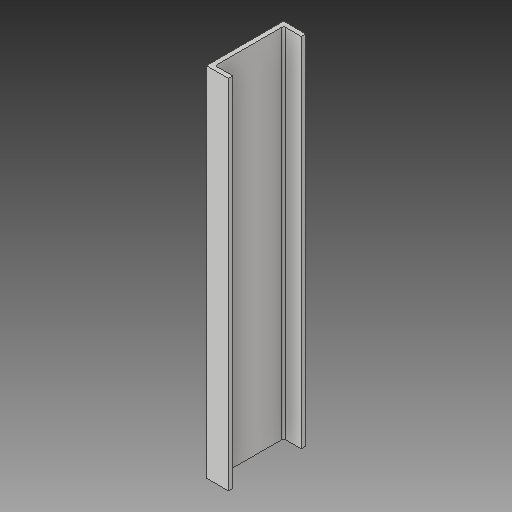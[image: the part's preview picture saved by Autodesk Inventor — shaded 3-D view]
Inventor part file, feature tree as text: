
AUTODESK INVENTOR PART (.ipt)
format: ipt  version: 2019 (Build 230136000, 136)  size: 122,368 bytes
history: native  units: mm
features: extrude x3, sketch x3, fillet x2
ambient origin geometry x8: Origin, YZ Plane, XZ Plane, XY Plane, X Axis, Y Axis, Z Axis, Center Point
bodies: Solid1 (feature_tree)
feature tree (8):
  extrude  "Extrusion1"  Depth=10.0mm
  extrude  "Extrusion2"  Depth=10.0mm
  extrude  "Extrusion3"  Depth=40.0mm TaperAngle=0.0deg
  fillet  "Fillet1"  Radius=155.0mm
  fillet  "Fillet2"  Radius=40.0mm
  sketch  "Sketch1"  dims[d2=10.0mm d3=0.0mm d4=10.0mm]
  sketch  "Sketch2"  dims[d5=10.0mm d6=10.0mm]
  sketch  "Sketch3"  dims[d7=10.0mm d8=40.0mm d9=0.0mm d10=155.0mm d11=40.0mm d12=0.0mm d13=4.0mm d14=4.0mm]
